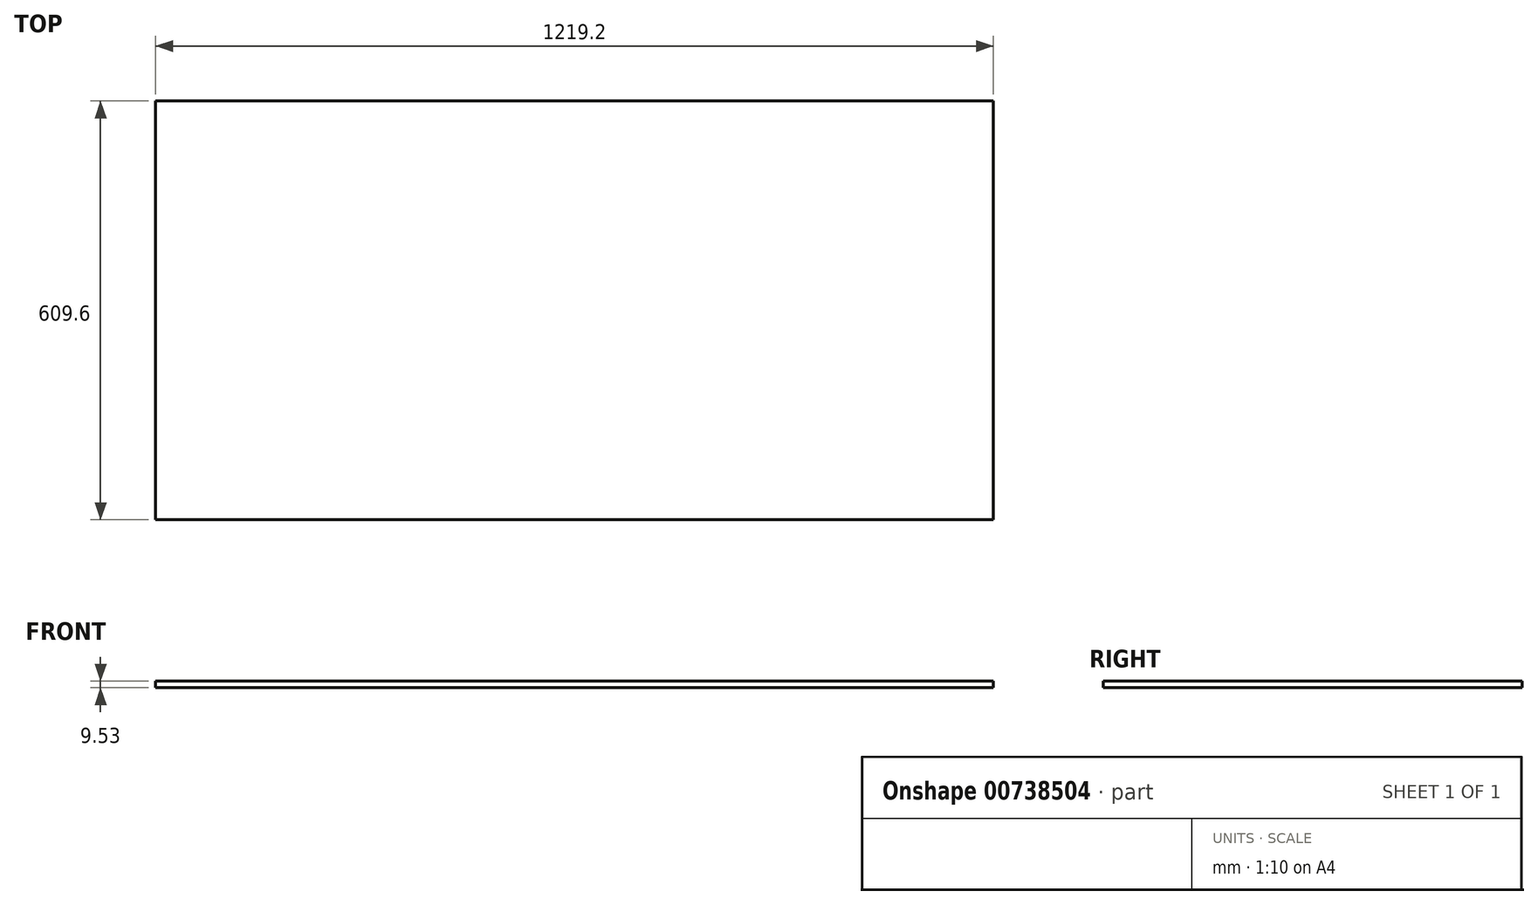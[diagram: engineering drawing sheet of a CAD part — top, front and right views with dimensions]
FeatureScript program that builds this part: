
annotation { "Feature Type Name" : "Feature", "Feature Type Description" : "" }
export const myFeature = defineFeature(function(context is Context, id is Id, definition is map)
    precondition{}
    {
        {
            var Q0;
            Q0=qCreatedBy(makeId("Top.planeOp"),FACE);
            var sketch = newSketch(context, id + "F0", { "sketchPlane" : qUnion([Q0])});
            skLineSegment(sketch, "E0.bottom", {"start": v(609.6, 304.8) * mm, "end": v(-609.6, 304.8) * mm});
            skLineSegment(sketch, "E0.top", {"start": v(609.6, -304.8) * mm, "end": v(-609.6, -304.8) * mm});
            skLineSegment(sketch, "E0.left", {"start": v(609.6, 304.8) * mm, "end": v(609.6, -304.8) * mm});
            skLineSegment(sketch, "E0.right", {"start": v(-609.6, 304.8) * mm, "end": v(-609.6, -304.8) * mm});
            skPoint(sketch, "E0.middle", {"position": v(0, 0) * mm});
            skSolve(sketch);
        }
        {
            var Q0;
            Q0 = qSketchRegion(id + "F0", true);
            extrude(context, id + "F1", {"entities" : qUnion([Q0]), "depth" : 9.52 * mm, "offsetDistance" : 25.4 * mm});
        }
    });
